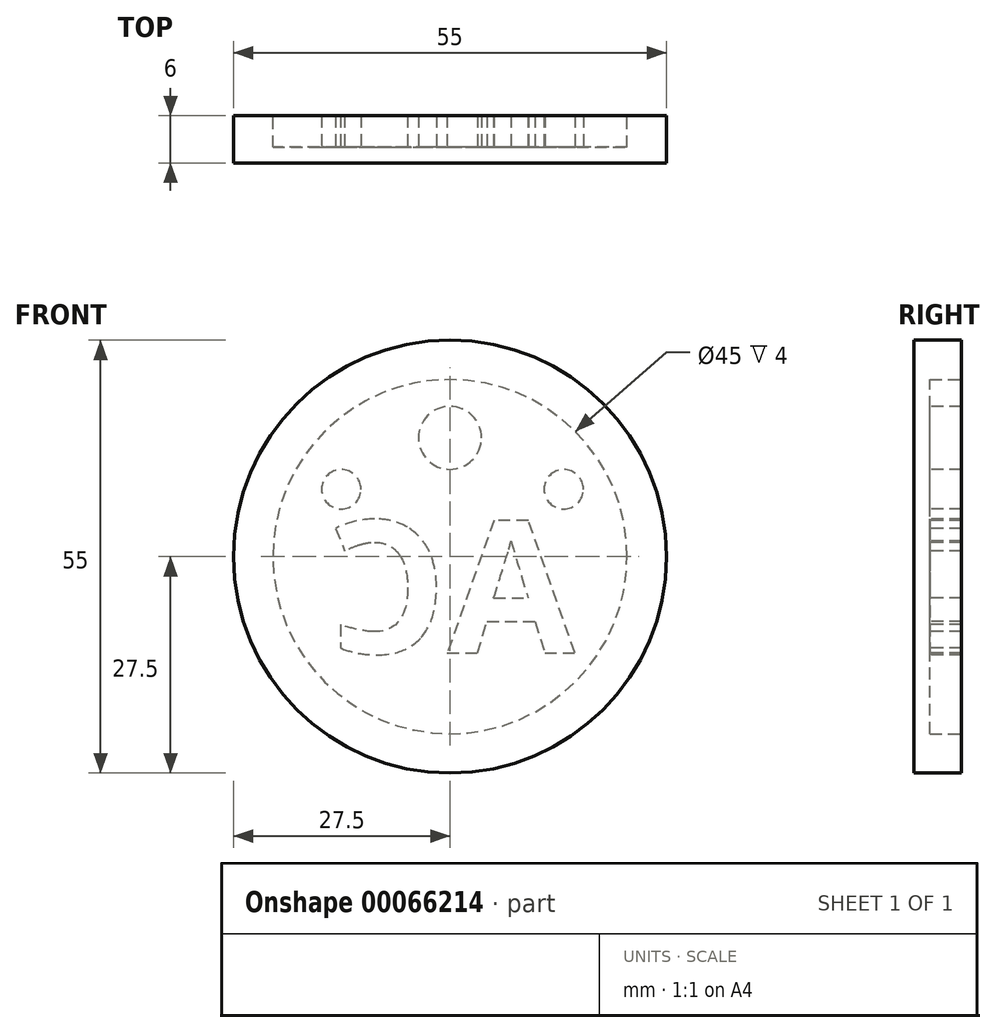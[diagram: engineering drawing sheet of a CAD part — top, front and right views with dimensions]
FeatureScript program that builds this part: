
annotation { "Feature Type Name" : "Feature", "Feature Type Description" : "" }
export const myFeature = defineFeature(function(context is Context, id is Id, definition is map)
    precondition{}
    {
        {
            var Q0;
            Q0=qCreatedBy(makeId("Front.planeOp"),FACE);
            var sketch = newSketch(context, id + "F0", { "sketchPlane" : qUnion([Q0])});
            skCircle(sketch, "E0", {"center": v(0, 0) * mm, "radius": 27.5 * mm});
            skSolve(sketch);
        }
        {
            var Q0;
            Q0 = qSketchRegion(id + "F0", true);
            extrude(context, id + "F1", {"entities" : qUnion([Q0]), "depth" : 6 * mm});
        }
        {
            var Q0;
            Q0=qCreatedBy(makeId("Front.planeOp"),FACE);
            var sketch = newSketch(context, id + "F2", { "sketchPlane" : qUnion([Q0])});
            skCircle(sketch, "E1", {"center": v(0, 0) * mm, "radius": 22.5 * mm});
            skSolve(sketch);
        }
        {
            var Q0;
            Q0 = qSketchRegion(id + "F2", true);
            extrude(context, id + "F3", {"entities" : qUnion([Q0]), "operationType" : NewBodyOperationType.REMOVE, "depth" : 4 * mm});
        }
        {
            var Q0;
            Q0=makeQuery(id+"F3.boolean.opBoolean","COPY",FACE,{"derivedFrom":makeQuery(id+"F3.opExtrude","CAP_FACE",FACE,{"disambiguationData":[OSD([sQuery(id+"F2.wireOp",EDGE,"E1")])],"isStart":false})});
            var sketch = newSketch(context, id + "F4", { "sketchPlane" : qUnion([Q0])});
            skCircle(sketch, "E2", {"center": v(-14.45, 8.56) * mm, "radius": 2.5 * mm});
            skCircle(sketch, "E3", {"center": v(0, 15.09) * mm, "radius": 4 * mm});
            skCircle(sketch, "E4", {"center": v(13.82, 8.56) * mm, "radius": 2.5 * mm});
            skText(sketch, "E5", { "text": "AC", "fontName": "OpenSans-Bold.ttf"});
            const initialGuessF4  = {"E5": [-0.01588, -0.01225, 1, 0, 0.01694]};
            skSetInitialGuess(sketch, initialGuessF4);
            skSolve(sketch);
        }
        {
            var Q0;
            Q0 = qSketchRegion(id + "F4", true);
            var Q1;
            Q1=makeQuery(id+"F1.opExtrude","CAP_FACE",FACE,{"disambiguationData":[OSD([sQuery(id+"F0.wireOp",EDGE,"E0")])],"isStart":true});
            extrude(context, id + "F5", {"entities" : qUnion([Q0]), "operationType" : NewBodyOperationType.ADD, "endBound" : BoundingType.UP_TO_SURFACE, "endBoundEntityFace" : qUnion([Q1]), "depth" : 25.4 * mm});
        }
    });
